# Revit family: 7KPAY0001A-18kW_01
name_source: partatom
category: Mechanical Equipment
units: mm (PartAtom-declared; Revit-internal decimal feet)

## family parameters
Always vertical = Yes
Classification Number = 23.65.35.11.14
Cut with Voids When Loaded = No
Host = Wall
Maintain Annotation Orientation = No
Part Type = Normal
Room Calculation Point = No
Round Connector Dimension = Use Radius
Shared = No

## types (4) — shared parameters
Actual Condensate Drain Flow = 0.0 GPM
Apparent Load = 0 VA
Assembly Code = D2020200
Case Material = Paint - Rheem - Case Paint - White
Condensate Connection Radius = 0' - 0 1/8"
Connector Material = Metal - Rheem - Connector Material - Brass
Default Elevation = 0' - 0"
Description = Tankless Water Heater
Edition number = 1
Gas Connection Radius = 0' - 0 3/8"
Gas Flow = 0.0 GPM
Heater Location = Outdoor
Heater Type = Condensing
Manufacturer = Rheem / Ruud / Raypak
Product Guid = df137c37-4a60-4d46-9e9e-45bd6ef4e6ee
Product data url = https://bimobject.com
URL = Rheem.com
Voltage = 120 V
Water Connection Radius = 0' - 0 3/8"
Water Flow = 4.9 GPM

## per-type parameters (varying)
| type | Fuel Type | Maximum Heating Input | Mounting Height | Raypak Model Number | Rheem Model Number | Ruud Model Number |
| 95XLN | NG | 199900 Btu/h | 4' - 6" | NH-209XLN | RUTG-95XLN | RTG-95XLN |
| 95XLP | LP | 199900 Btu/h | 4' - 0" | NH-209XLP | RUTG-95XLP | RTG-95XLP |
| 84XLN | NG | 157000 Btu/h | 4' - 0" | NH-159XLN | RUTG-84XLN | RTG-84XLN |
| 84XLP | LP | 157000 Btu/h | 4' - 0" | NH-159XLP | RUTG-84XLP | RTG-84XLP |

note: column(s) folded — value = type name in every type: Model

## geometry (parser evidence)
native form markers: Blend x10, Sweep x2
no freeform markers — native parametric forms only
